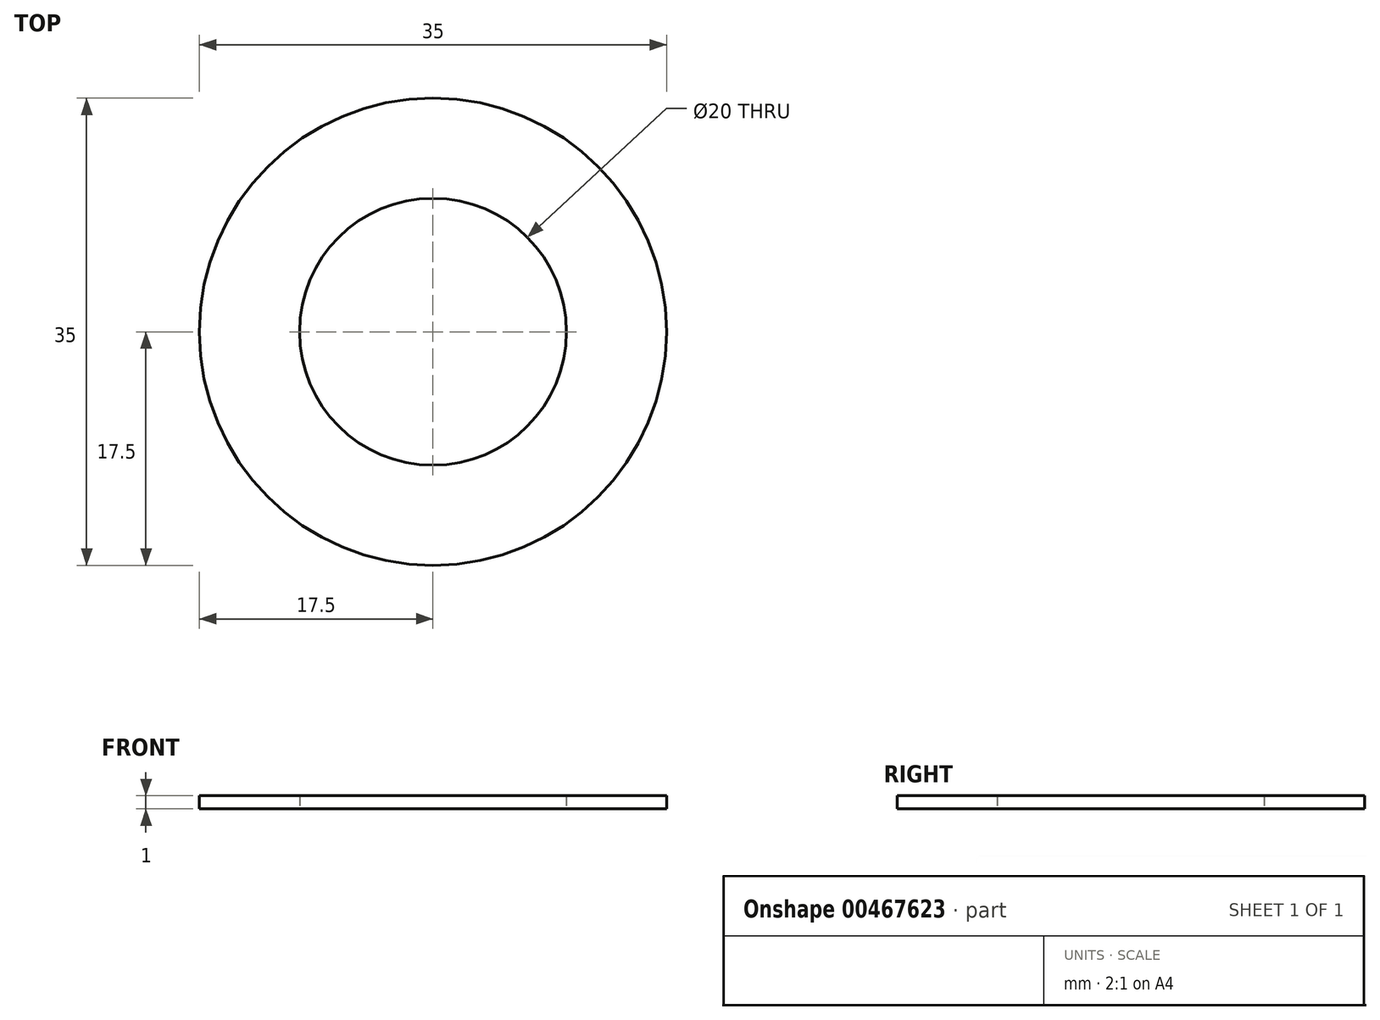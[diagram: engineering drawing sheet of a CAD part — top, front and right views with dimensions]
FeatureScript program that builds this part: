
annotation { "Feature Type Name" : "Feature", "Feature Type Description" : "" }
export const myFeature = defineFeature(function(context is Context, id is Id, definition is map)
    precondition{}
    {
        {
            var Q0;
            Q0=qCreatedBy(makeId("Top.planeOp"),FACE);
            var sketch = newSketch(context, id + "F0", { "sketchPlane" : qUnion([Q0])});
            skCircle(sketch, "E0", {"center": v(0, 0) * mm, "radius": 17.5 * mm});
            skCircle(sketch, "E1", {"center": v(0, 0) * mm, "radius": 10 * mm});
            skSolve(sketch);
        }
        {
            var Q0;
            Q0=makeQuery(id+"F0.imprint","IMPRINT",FACE,{"disambiguationData":[TD([[makeQuery(id+"F0.imprint","IMPRINT",EDGE,{"derivedFrom":sQuery(id+"F0.wireOp",EDGE,"E0")}),1.0]])]});
            extrude(context, id + "F1", {"entities" : qUnion([Q0]), "depth" : 1 * mm});
        }
    });
